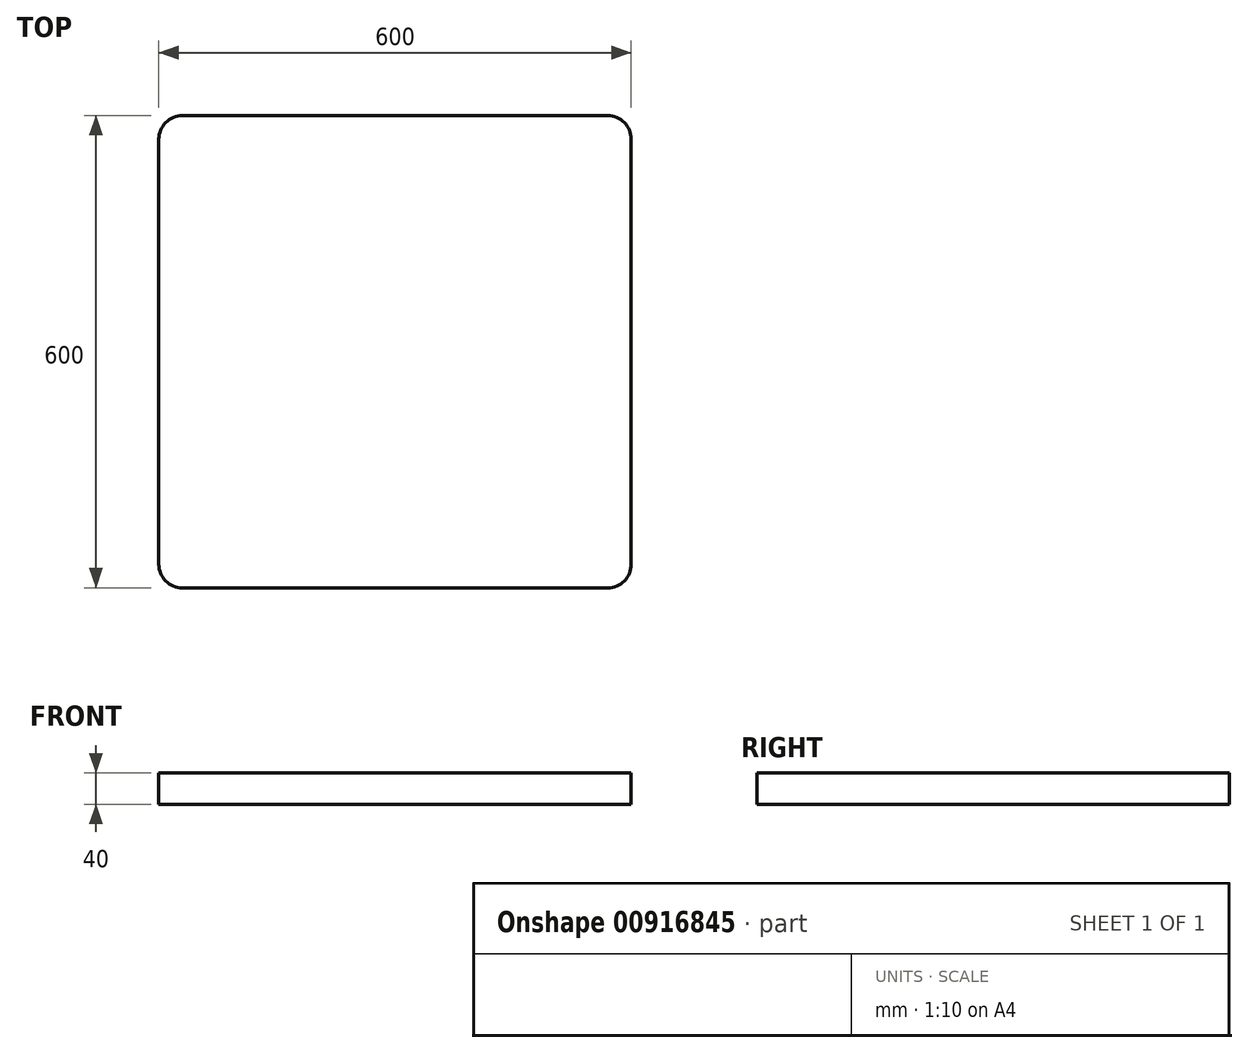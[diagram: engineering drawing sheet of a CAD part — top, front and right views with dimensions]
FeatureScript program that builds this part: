
annotation { "Feature Type Name" : "Feature", "Feature Type Description" : "" }
export const myFeature = defineFeature(function(context is Context, id is Id, definition is map)
    precondition{}
    {
        {
            var Q0;
            Q0=qCreatedBy(makeId("Top.planeOp"),FACE);
            var sketch = newSketch(context, id + "F0", { "sketchPlane" : qUnion([Q0])});
            skLineSegment(sketch, "E0.bottom", {"start": v(-300, 300) * mm, "end": v(300, 300) * mm});
            skLineSegment(sketch, "E0.top", {"start": v(-300, -300) * mm, "end": v(300, -300) * mm});
            skLineSegment(sketch, "E0.left", {"start": v(-300, 300) * mm, "end": v(-300, -300) * mm});
            skLineSegment(sketch, "E0.right", {"start": v(300, 300) * mm, "end": v(300, -300) * mm});
            skPoint(sketch, "E0.middle", {"position": v(0, 0) * mm});
            skSolve(sketch);
        }
        {
            var Q0;
            Q0=qSketchRegion(id+"F0",true);
            extrude(context, id + "F1", {"entities" : qUnion([Q0]), "depth" : 40 * mm, "offsetDistance" : 25 * mm});
        }
        {
            var Q0;
            Q0=makeQuery(id+"F1.opExtrude","SWEPT_EDGE",EDGE,{"disambiguationData":[OSD([sQuery(id+"F0.wireOp",EDGE,"E0.bottom"),sQuery(id+"F0.wireOp",EDGE,"E0.right")])]});
            var Q1;
            Q1=makeQuery(id+"F1.opExtrude","SWEPT_EDGE",EDGE,{"disambiguationData":[OSD([sQuery(id+"F0.wireOp",EDGE,"E0.bottom"),sQuery(id+"F0.wireOp",EDGE,"E0.left")])]});
            var Q2;
            Q2=makeQuery(id+"F1.opExtrude","SWEPT_EDGE",EDGE,{"disambiguationData":[OSD([sQuery(id+"F0.wireOp",EDGE,"E0.top"),sQuery(id+"F0.wireOp",EDGE,"E0.left")])]});
            var Q3;
            Q3=makeQuery(id+"F1.opExtrude","SWEPT_EDGE",EDGE,{"disambiguationData":[OSD([sQuery(id+"F0.wireOp",EDGE,"E0.top"),sQuery(id+"F0.wireOp",EDGE,"E0.right")])]});
            fillet(context, id + "F2", {"entities" : qUnion([Q0, Q1, Q2, Q3]), "radius" : 30 * mm, "tangentPropagation" : true, "allowEdgeOverflow" : false});
        }
    });
